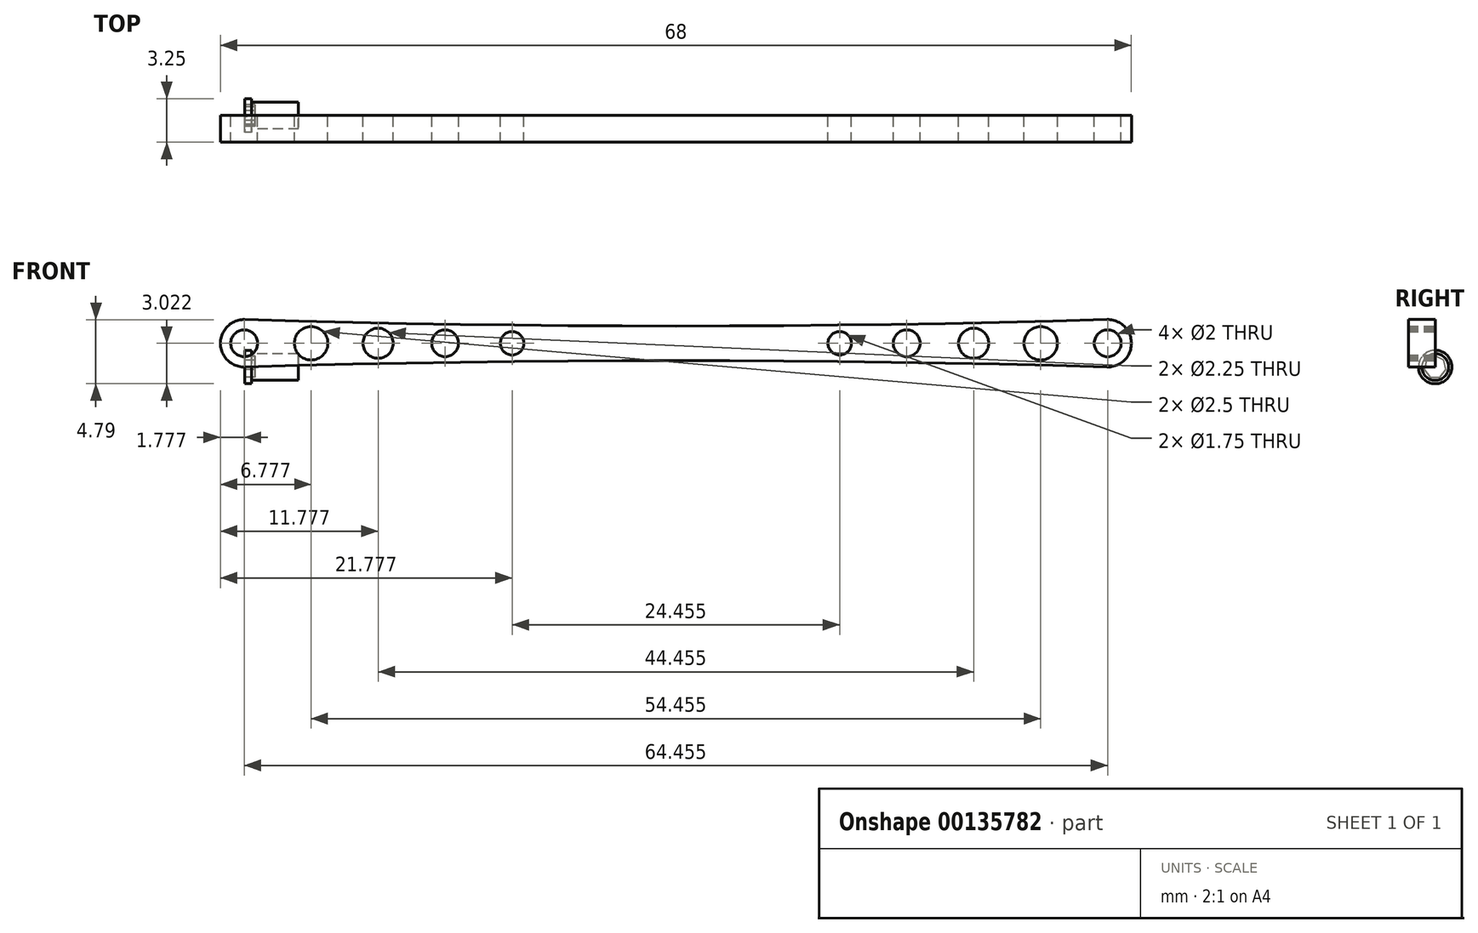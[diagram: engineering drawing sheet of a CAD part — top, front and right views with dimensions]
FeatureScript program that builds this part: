
annotation { "Feature Type Name" : "Feature", "Feature Type Description" : "" }
export const myFeature = defineFeature(function(context is Context, id is Id, definition is map)
    precondition{}
    {
        {
            var Q0;
            Q0=qCreatedBy(makeId("Front.planeOp"),FACE);
            var sketch = newSketch(context, id + "F0", { "sketchPlane" : qUnion([Q0])});
            skArc(sketch, "E0", {"start": v(0, 3.54) * mm, "mid": v(-1.83, 1.77) * mm, "end": v(0, 0) * mm});
            skArc(sketch, "E1", {"start": v(64.35, 0) * mm, "mid": v(66.17, 1.77) * mm, "end": v(64.35, 3.54) * mm});
            skArc(sketch, "E2", {"start": v(0, 3.54) * mm, "mid": v(32.17, 3.06) * mm, "end": v(64.35, 3.54) * mm});
            skArc(sketch, "E3", {"start": v(64.35, 0) * mm, "mid": v(32.17, 0.48) * mm, "end": v(0, 0) * mm});
            skCircle(sketch, "E4", {"center": v(-0.05, 1.77) * mm, "radius": 1 * mm});
            skCircle(sketch, "E5", {"center": v(64.4, 1.77) * mm, "radius": 1 * mm});
            skLineSegment(sketch, "E6", {"start": v(-0.05, 1.77) * mm, "end": v(64.4, 1.77) * mm, "construction": true});
            skCircle(sketch, "E7", {"center": v(4.95, 1.77) * mm, "radius": 1.25 * mm});
            skCircle(sketch, "E8", {"center": v(9.95, 1.77) * mm, "radius": 1.13 * mm});
            skCircle(sketch, "E9", {"center": v(14.95, 1.77) * mm, "radius": 1 * mm});
            skCircle(sketch, "E10", {"center": v(19.95, 1.77) * mm, "radius": 0.88 * mm});
            skCircle(sketch, "E11", {"center": v(59.4, 1.77) * mm, "radius": 1.25 * mm});
            skCircle(sketch, "E12", {"center": v(54.4, 1.77) * mm, "radius": 1.13 * mm});
            skCircle(sketch, "E13", {"center": v(49.4, 1.77) * mm, "radius": 1 * mm});
            skCircle(sketch, "E14", {"center": v(44.4, 1.77) * mm, "radius": 0.88 * mm});
            skSolve(sketch);
        }
        {
            var Q0;
            Q0 = qSketchRegion(id + "F0", true);
            extrude(context, id + "F1", {"entities" : qUnion([Q0]), "depth" : 2 * mm});
        }
        {
            var Q0;
            Q0=qCreatedBy(makeId("Front.planeOp"),FACE);
            var sketch = newSketch(context, id + "F2", { "sketchPlane" : qUnion([Q0])});
            skLineSegment(sketch, "E15", {"start": v(-3.37, 0) * mm, "end": v(6.86, 0) * mm, "construction": true});
            skLineSegment(sketch, "E16", {"start": v(0, 0) * mm, "end": v(0, 1.25) * mm});
            skLineSegment(sketch, "E17", {"start": v(0, 1.25) * mm, "end": v(0.5, 1.25) * mm});
            skLineSegment(sketch, "E18", {"start": v(0.5, 1.25) * mm, "end": v(0.5, 1) * mm});
            skLineSegment(sketch, "E19", {"start": v(0.5, 1) * mm, "end": v(4, 1) * mm});
            skLineSegment(sketch, "E20", {"start": v(4, 1) * mm, "end": v(4, 0) * mm});
            skLineSegment(sketch, "E21", {"start": v(4, 0) * mm, "end": v(0, 0) * mm});
            skSolve(sketch);
        }
        {
            var Q0;
            Q0=makeQuery(id+"F2.imprint","IMPRINT",FACE,{"disambiguationData":[TD([[makeQuery(id+"F2.imprint","IMPRINT",EDGE,{"derivedFrom":sQuery(id+"F2.wireOp",EDGE,"E16")}),-1.0]])]});
            var Q1;
            Q1=sQuery(id+"F2.wireOp",EDGE,"E15");
            revolve(context, id + "F3", {"entities" : qUnion([Q0]), "axis" : qUnion([Q1]), "revolveType" : RevolveType.FULL});
        }
        {
            var Q0;
            Q0=makeQuery(id+"F3.opRevolve","SWEPT_FACE",FACE,{"disambiguationData":[OSD([sQuery(id+"F2.wireOp",EDGE,"E16")])]});
            var sketch = newSketch(context, id + "F4", { "sketchPlane" : qUnion([Q0])});
            skCircle(sketch, "E22.cCircle", {"center": v(0, 0) * mm, "radius": 0.75 * mm, "construction": true});
            skLineSegment(sketch, "E22.0", {"start": v(0.81, -0.18) * mm, "end": v(0.36, -0.75) * mm});
            skLineSegment(sketch, "E22.1", {"start": v(0.36, -0.75) * mm, "end": v(-0.36, -0.75) * mm});
            skLineSegment(sketch, "E22.2", {"start": v(-0.36, -0.75) * mm, "end": v(-0.81, -0.19) * mm});
            skLineSegment(sketch, "E22.3", {"start": v(-0.81, -0.19) * mm, "end": v(-0.65, 0.52) * mm});
            skLineSegment(sketch, "E22.4", {"start": v(-0.65, 0.52) * mm, "end": v(0, 0.83) * mm});
            skLineSegment(sketch, "E22.5", {"start": v(0, 0.83) * mm, "end": v(0.65, 0.52) * mm});
            skLineSegment(sketch, "E22.6", {"start": v(0.65, 0.52) * mm, "end": v(0.81, -0.18) * mm});
            skPoint(sketch, "E22.0.midPoint", {"position": v(0.59, -0.47) * mm});
            skSolve(sketch);
        }
        {
            var Q0;
            Q0=makeQuery(id+"F4.imprint","IMPRINT",FACE,{"disambiguationData":[TD([[makeQuery(id+"F4.imprint","IMPRINT",EDGE,{"derivedFrom":sQuery(id+"F4.wireOp",EDGE,"E22.0")}),-1.0]])]});
            extrude(context, id + "F5", {"entities" : qUnion([Q0]), "operationType" : NewBodyOperationType.REMOVE, "oppositeDirection" : true, "depth" : .75 * mm});
        }
    });
